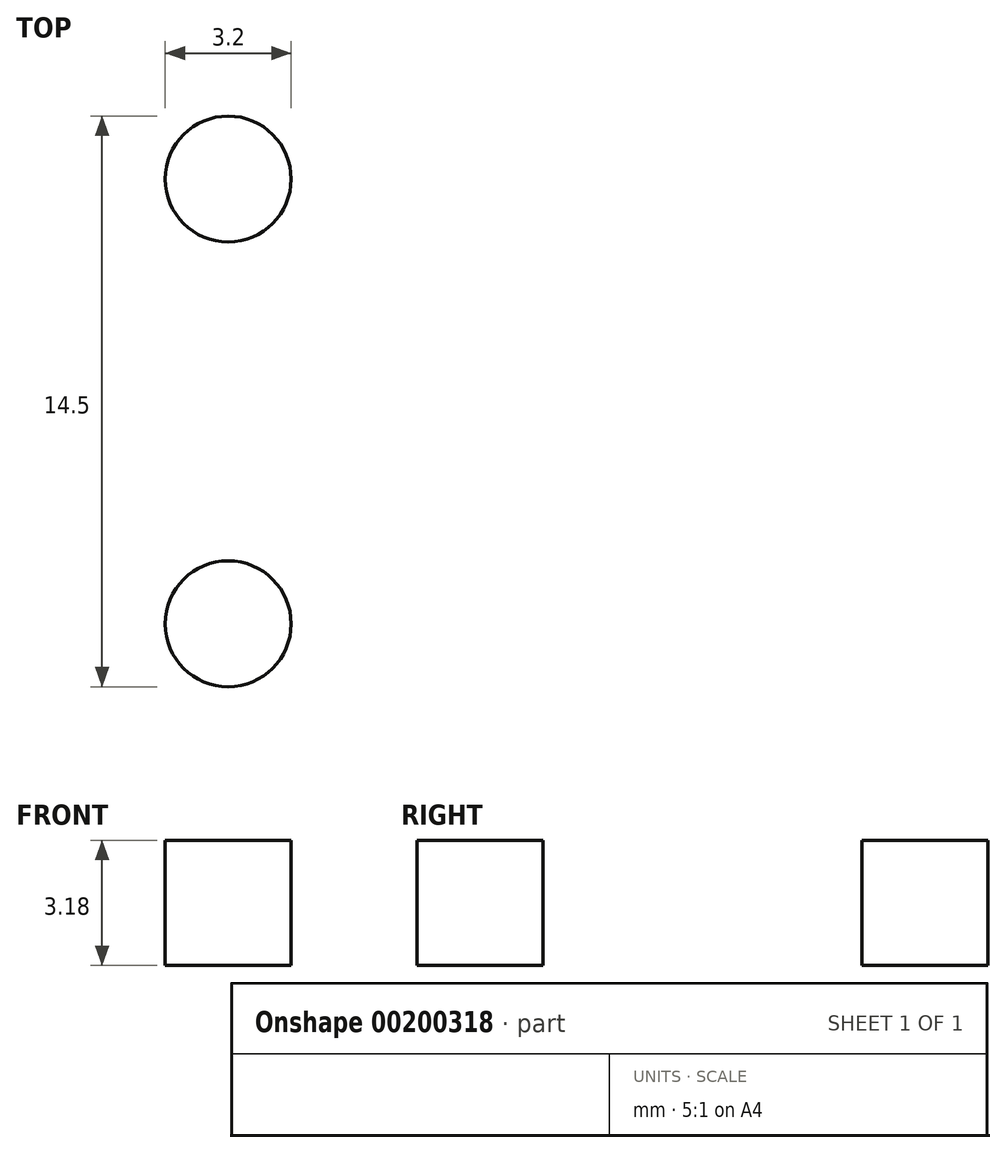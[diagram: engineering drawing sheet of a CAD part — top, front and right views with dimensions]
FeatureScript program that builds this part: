
annotation { "Feature Type Name" : "Feature", "Feature Type Description" : "" }
export const myFeature = defineFeature(function(context is Context, id is Id, definition is map)
    precondition{}
    {
        {
            var Q0;
            Q0=qCreatedBy(makeId("Top.planeOp"),FACE);
            var sketch = newSketch(context, id + "F0", { "sketchPlane" : qUnion([Q0])});
            skLineSegment(sketch, "E0.bottom", {"start": v(-57, -18.18) * mm, "end": v(57, -18.18) * mm});
            skLineSegment(sketch, "E0.top", {"start": v(-57, 18.18) * mm, "end": v(57, 18.18) * mm});
            skLineSegment(sketch, "E0.left", {"start": v(-57, -18.18) * mm, "end": v(-57, 18.18) * mm});
            skLineSegment(sketch, "E0.right", {"start": v(57, -18.18) * mm, "end": v(57, 18.18) * mm});
            skPoint(sketch, "E0.middle", {"position": v(0, 0) * mm});
            skSolve(sketch);
        }
        {
            var Q0;
            Q0=makeQuery(id+"F0.imprint","IMPRINT",FACE,{"disambiguationData":[TD([[makeQuery(id+"F0.imprint","IMPRINT",EDGE,{"derivedFrom":sQuery(id+"F0.wireOp",EDGE,"E0.bottom")}),1.0]])]});
            extrude(context, id + "F1", {"entities" : qUnion([Q0]), "depth" : 3.17 * mm});
        }
        {
            var Q0;
            Q0=makeQuery(id+"F1.opExtrude","CAP_FACE",FACE,{"disambiguationData":[OSD([sQuery(id+"F0.wireOp",EDGE,"E0.bottom"),sQuery(id+"F0.wireOp",EDGE,"E0.top"),sQuery(id+"F0.wireOp",EDGE,"E0.left"),sQuery(id+"F0.wireOp",EDGE,"E0.right")])],"isStart":false});
            var sketch = newSketch(context, id + "F2", { "sketchPlane" : qUnion([Q0])});
            skLineSegment(sketch, "E1.bottom", {"start": v(-57, 18.18) * mm, "end": v(-47.65, 18.18) * mm, "construction": true});
            skLineSegment(sketch, "E1.top", {"start": v(-57, 5.65) * mm, "end": v(-47.65, 5.65) * mm, "construction": true});
            skLineSegment(sketch, "E1.left", {"start": v(-57, 18.18) * mm, "end": v(-57, 5.65) * mm, "construction": true});
            skLineSegment(sketch, "E1.right", {"start": v(-47.65, 18.18) * mm, "end": v(-47.65, 5.65) * mm, "construction": true});
            skCircle(sketch, "E2", {"center": v(-47.65, 5.65) * mm, "radius": 1.6 * mm});
            skCircle(sketch, "E3.MirrorC", {"center": v(47.65, 5.65) * mm, "radius": 1.6 * mm});
            skLineSegment(sketch, "E4.bottom", {"start": v(-57, -18.18) * mm, "end": v(-47.65, -18.18) * mm, "construction": true});
            skLineSegment(sketch, "E4.top", {"start": v(-57, -5.65) * mm, "end": v(-47.65, -5.65) * mm, "construction": true});
            skLineSegment(sketch, "E4.left", {"start": v(-57, -18.18) * mm, "end": v(-57, -5.65) * mm, "construction": true});
            skLineSegment(sketch, "E4.right", {"start": v(-47.65, -18.18) * mm, "end": v(-47.65, -5.65) * mm, "construction": true});
            skCircle(sketch, "E5", {"center": v(-47.65, -5.65) * mm, "radius": 1.6 * mm});
            skCircle(sketch, "E6.MirrorC", {"center": v(47.65, -5.65) * mm, "radius": 1.6 * mm});
            skSolve(sketch);
        }
        {
            var Q0;
            Q0=makeQuery(id+"F2.imprint","IMPRINT",FACE,{"disambiguationData":[TD([[makeQuery(id+"F2.imprint","IMPRINT",EDGE,{"derivedFrom":sQuery(id+"F2.wireOp",EDGE,"E2")}),1.0]])]});
            var Q1;
            Q1=makeQuery(id+"F2.imprint","IMPRINT",FACE,{"disambiguationData":[TD([[makeQuery(id+"F2.imprint","IMPRINT",EDGE,{"derivedFrom":sQuery(id+"F2.wireOp",EDGE,"E5")}),1.0]])]});
            var Q2;
            Q2=makeQuery(id+"F2.imprint","IMPRINT",FACE,{"disambiguationData":[TD([[makeQuery(id+"F2.imprint","IMPRINT",EDGE,{"derivedFrom":sQuery(id+"F2.wireOp",EDGE,"E6.MirrorC")}),-1.0]])]});
            var Q3;
            Q3=makeQuery(id+"F2.imprint","IMPRINT",FACE,{"disambiguationData":[TD([[makeQuery(id+"F2.imprint","IMPRINT",EDGE,{"derivedFrom":sQuery(id+"F2.wireOp",EDGE,"E3.MirrorC")}),-1.0]])]});
            extrude(context, id + "F3", {"entities" : qUnion([Q0, Q1, Q2, Q3]), "operationType" : NewBodyOperationType.REMOVE, "oppositeDirection" : true, "depth" : 25 * mm});
        }
    });
